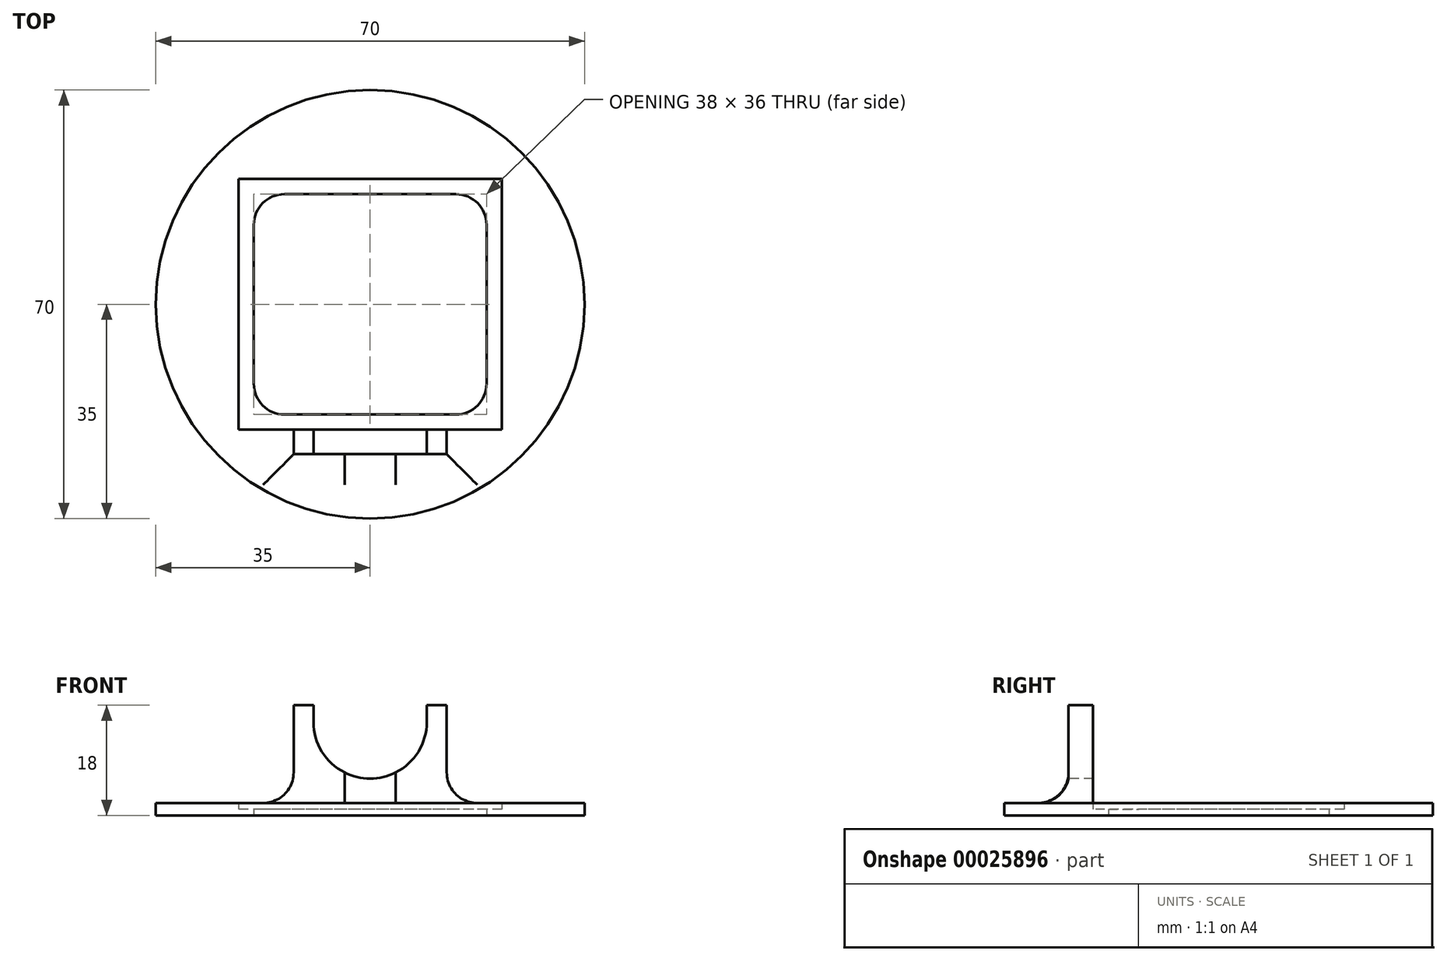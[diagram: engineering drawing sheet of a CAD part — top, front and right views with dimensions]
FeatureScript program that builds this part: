
annotation { "Feature Type Name" : "Feature", "Feature Type Description" : "" }
export const myFeature = defineFeature(function(context is Context, id is Id, definition is map)
    precondition{}
    {
        {
            var Q0;
            Q0=qCreatedBy(makeId("Top.planeOp"),FACE);
            var sketch = newSketch(context, id + "F0", { "sketchPlane" : qUnion([Q0])});
            skCircle(sketch, "E0", {"center": v(0, 0) * mm, "radius": 35 * mm});
            skLineSegment(sketch, "E1.bottom", {"start": v(21.5, 20.5) * mm, "end": v(-21.5, 20.5) * mm});
            skLineSegment(sketch, "E1.top", {"start": v(21.5, -20.5) * mm, "end": v(-21.5, -20.5) * mm});
            skLineSegment(sketch, "E1.left", {"start": v(21.5, 20.5) * mm, "end": v(21.5, -20.5) * mm});
            skLineSegment(sketch, "E1.right", {"start": v(-21.5, 20.5) * mm, "end": v(-21.5, -20.5) * mm});
            skSolve(sketch);
        }
        {
            var Q0;
            Q0=makeQuery(id+"F0.imprint","IMPRINT",FACE,{"disambiguationData":[TD([[makeQuery(id+"F0.imprint","IMPRINT",EDGE,{"derivedFrom":sQuery(id+"F0.wireOp",EDGE,"E0")}),1.0]])]});
            extrude(context, id + "F1", {"entities" : qUnion([Q0]), "depth" : 2 * mm, "offsetDistance" : 25 * mm});
        }
        {
            var Q0;
            Q0=qCreatedBy(makeId("Top.planeOp"),FACE);
            var sketch = newSketch(context, id + "F2", { "sketchPlane" : qUnion([Q0])});
            skLineSegment(sketch, "E2.bottom", {"start": v(12.5, -20.5) * mm, "end": v(-12.5, -20.5) * mm});
            skLineSegment(sketch, "E2.top", {"start": v(12.5, -24.5) * mm, "end": v(-12.5, -24.5) * mm});
            skLineSegment(sketch, "E2.left", {"start": v(12.5, -20.5) * mm, "end": v(12.5, -24.5) * mm});
            skLineSegment(sketch, "E2.right", {"start": v(-12.5, -20.5) * mm, "end": v(-12.5, -24.5) * mm});
            skPoint(sketch, "E2.middle", {"position": v(0, -22.5) * mm});
            skSolve(sketch);
        }
        {
            var Q0;
            Q0 = qSketchRegion(id + "F2", true);
            extrude(context, id + "F3", {"entities" : qUnion([Q0]), "operationType" : NewBodyOperationType.ADD, "depth" : 18 * mm, "offsetDistance" : 25 * mm});
        }
        {
            var Q0;
            Q0=makeQuery(id+"F3.opExtrude","SWEPT_FACE",FACE,{"disambiguationData":[OSD([sQuery(id+"F2.wireOp",EDGE,"E2.top")])]});
            var sketch = newSketch(context, id + "F4", { "sketchPlane" : qUnion([Q0])});
            skArc(sketch, "E3", {"start": v(-9.25, 15.25) * mm, "mid": v(0, 6) * mm, "end": v(9.25, 15.25) * mm});
            skLineSegment(sketch, "E4", {"start": v(-9.25, 15.25) * mm, "end": v(-9.25, 18) * mm});
            skLineSegment(sketch, "E5", {"start": v(9.25, 15.25) * mm, "end": v(9.25, 18) * mm});
            skLineSegment(sketch, "E6", {"start": v(9.25, 18) * mm, "end": v(-9.25, 18) * mm});
            skSolve(sketch);
        }
        {
            var Q0;
            Q0 = qSketchRegion(id + "F4", true);
            extrude(context, id + "F5", {"entities" : qUnion([Q0]), "operationType" : NewBodyOperationType.REMOVE, "endBound" : BoundingType.THROUGH_ALL, "oppositeDirection" : true, "depth" : 25 * mm, "offsetDistance" : 25 * mm});
        }
        {
            var Q0;
            Q0=qCreatedBy(makeId("Top.planeOp"),FACE);
            var sketch = newSketch(context, id + "F6", { "sketchPlane" : qUnion([Q0])});
            skLineSegment(sketch, "E7.0", {"start": v(-19, 18) * mm, "end": v(-19, -18) * mm});
            skLineSegment(sketch, "E7.1", {"start": v(19, 18) * mm, "end": v(-19, 18) * mm});
            skLineSegment(sketch, "E7.2", {"start": v(19, 18) * mm, "end": v(19, -18) * mm});
            skLineSegment(sketch, "E7.3", {"start": v(19, -18) * mm, "end": v(-19, -18) * mm});
            skLineSegment(sketch, "E8.0", {"start": v(-21.5, 20.5) * mm, "end": v(-21.5, -20.5) * mm});
            skLineSegment(sketch, "E9.0", {"start": v(21.5, 20.5) * mm, "end": v(-21.5, 20.5) * mm});
            skLineSegment(sketch, "E10.0", {"start": v(21.5, 20.5) * mm, "end": v(21.5, -20.5) * mm});
            skLineSegment(sketch, "E11.0", {"start": v(21.5, -20.5) * mm, "end": v(-21.5, -20.5) * mm});
            skSolve(sketch);
        }
        {
            var Q0;
            Q0 = qSketchRegion(id + "F6", true);
            extrude(context, id + "F7", {"entities" : qUnion([Q0]), "operationType" : NewBodyOperationType.ADD, "depth" : 1 * mm, "offsetDistance" : 25 * mm});
        }
        {
            var Q0;
            Q0=makeQuery(id+"F7.opExtrude","SWEPT_EDGE",EDGE,{"disambiguationData":[OSD([sQuery(id+"F6.wireOp",EDGE,"E7.0"),sQuery(id+"F6.wireOp",EDGE,"E7.1")])]});
            var Q1;
            Q1=makeQuery(id+"F7.opExtrude","SWEPT_EDGE",EDGE,{"disambiguationData":[OSD([sQuery(id+"F6.wireOp",EDGE,"E7.1"),sQuery(id+"F6.wireOp",EDGE,"E7.2")])]});
            var Q2;
            Q2=makeQuery(id+"F7.opExtrude","SWEPT_EDGE",EDGE,{"disambiguationData":[OSD([sQuery(id+"F6.wireOp",EDGE,"E7.2"),sQuery(id+"F6.wireOp",EDGE,"E7.3")])]});
            var Q3;
            Q3=makeQuery(id+"F7.opExtrude","SWEPT_EDGE",EDGE,{"disambiguationData":[OSD([sQuery(id+"F6.wireOp",EDGE,"E7.0"),sQuery(id+"F6.wireOp",EDGE,"E7.3")])]});
            fillet(context, id + "F8", {"entities" : qUnion([Q0, Q1, Q2, Q3]), "radius" : 5 * mm, "tangentPropagation" : true, "allowEdgeOverflow" : false});
        }
        {
            var Q0;
            Q0=makeQuery(id+"FxtIpcVDqsALg0z_1.1.F3.boolean.opBoolean","INTERSECT",EDGE,{"derivedFrom":[makeQuery(id+"F1.opExtrude","CAP_FACE",FACE,{"disambiguationData":[OSD([sQuery(id+"F0.wireOp",EDGE,"E0"),sQuery(id+"F0.wireOp",EDGE,"E1.bottom"),sQuery(id+"F0.wireOp",EDGE,"E1.top"),sQuery(id+"F0.wireOp",EDGE,"E1.left"),sQuery(id+"F0.wireOp",EDGE,"E1.right")])],"isStart":false}),makeQuery(id+"FxtIpcVDqsALg0z_1.1.F3.opExtrude","SWEPT_FACE",FACE,{"disambiguationData":[OSD([sQuery(id+"F2.wireOp",EDGE,"E2.left")])]})]});
            var Q1;
            Q1=makeQuery(id+"FxtIpcVDqsALg0z_1.1.F3.boolean.opBoolean","INTERSECT",EDGE,{"derivedFrom":[makeQuery(id+"F1.opExtrude","CAP_FACE",FACE,{"disambiguationData":[OSD([sQuery(id+"F0.wireOp",EDGE,"E0"),sQuery(id+"F0.wireOp",EDGE,"E1.bottom"),sQuery(id+"F0.wireOp",EDGE,"E1.top"),sQuery(id+"F0.wireOp",EDGE,"E1.left"),sQuery(id+"F0.wireOp",EDGE,"E1.right")])],"isStart":false}),makeQuery(id+"FxtIpcVDqsALg0z_1.1.F3.opExtrude","SWEPT_FACE",FACE,{"disambiguationData":[OSD([sQuery(id+"F2.wireOp",EDGE,"E2.top")])]})]});
            var Q2;
            Q2=makeQuery(id+"FxtIpcVDqsALg0z_1.1.F3.boolean.opBoolean","INTERSECT",EDGE,{"derivedFrom":[makeQuery(id+"F1.opExtrude","CAP_FACE",FACE,{"disambiguationData":[OSD([sQuery(id+"F0.wireOp",EDGE,"E0"),sQuery(id+"F0.wireOp",EDGE,"E1.bottom"),sQuery(id+"F0.wireOp",EDGE,"E1.top"),sQuery(id+"F0.wireOp",EDGE,"E1.left"),sQuery(id+"F0.wireOp",EDGE,"E1.right")])],"isStart":false}),makeQuery(id+"FxtIpcVDqsALg0z_1.1.F3.opExtrude","SWEPT_FACE",FACE,{"disambiguationData":[OSD([sQuery(id+"F2.wireOp",EDGE,"E2.right")])]})]});
            var Q3;
            Q3=makeQuery(id+"F3.boolean.opBoolean","INTERSECT",EDGE,{"derivedFrom":[makeQuery(id+"F1.opExtrude","CAP_FACE",FACE,{"disambiguationData":[OSD([sQuery(id+"F0.wireOp",EDGE,"E0"),sQuery(id+"F0.wireOp",EDGE,"E1.bottom"),sQuery(id+"F0.wireOp",EDGE,"E1.top"),sQuery(id+"F0.wireOp",EDGE,"E1.left"),sQuery(id+"F0.wireOp",EDGE,"E1.right")])],"isStart":false}),makeQuery(id+"F3.opExtrude","SWEPT_FACE",FACE,{"disambiguationData":[OSD([sQuery(id+"F2.wireOp",EDGE,"E2.right")])]})]});
            var Q4;
            Q4=makeQuery(id+"F3.boolean.opBoolean","INTERSECT",EDGE,{"derivedFrom":[makeQuery(id+"F1.opExtrude","CAP_FACE",FACE,{"disambiguationData":[OSD([sQuery(id+"F0.wireOp",EDGE,"E0"),sQuery(id+"F0.wireOp",EDGE,"E1.bottom"),sQuery(id+"F0.wireOp",EDGE,"E1.top"),sQuery(id+"F0.wireOp",EDGE,"E1.left"),sQuery(id+"F0.wireOp",EDGE,"E1.right")])],"isStart":false}),makeQuery(id+"F3.opExtrude","SWEPT_FACE",FACE,{"disambiguationData":[OSD([sQuery(id+"F2.wireOp",EDGE,"E2.top")])]})]});
            var Q5;
            Q5=makeQuery(id+"F3.boolean.opBoolean","INTERSECT",EDGE,{"derivedFrom":[makeQuery(id+"F1.opExtrude","CAP_FACE",FACE,{"disambiguationData":[OSD([sQuery(id+"F0.wireOp",EDGE,"E0"),sQuery(id+"F0.wireOp",EDGE,"E1.bottom"),sQuery(id+"F0.wireOp",EDGE,"E1.top"),sQuery(id+"F0.wireOp",EDGE,"E1.left"),sQuery(id+"F0.wireOp",EDGE,"E1.right")])],"isStart":false}),makeQuery(id+"F3.opExtrude","SWEPT_FACE",FACE,{"disambiguationData":[OSD([sQuery(id+"F2.wireOp",EDGE,"E2.left")])]})]});
            fillet(context, id + "F9", {"entities" : qUnion([Q0, Q1, Q2, Q3, Q4, Q5]), "radius" : 5 * mm, "tangentPropagation" : true, "allowEdgeOverflow" : false});
        }
    });
